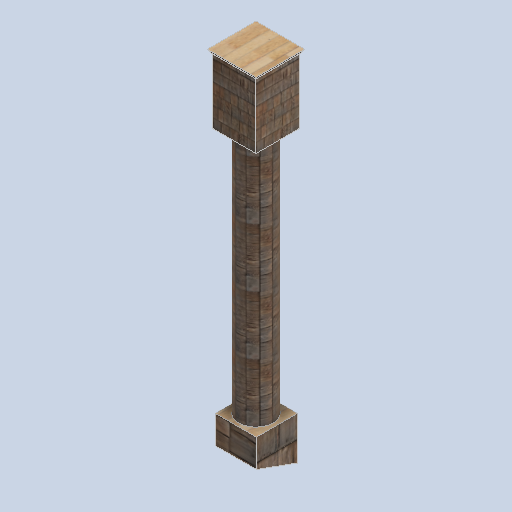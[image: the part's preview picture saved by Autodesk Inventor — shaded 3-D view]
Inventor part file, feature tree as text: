
AUTODESK INVENTOR PART (.ipt)
format: ipt  version: 2024.2 (Build 282272000, 272)  size: 172,544 bytes
history: native  units: in
note: dims shown in document units (in); Inventor stores cm internally (conversion verified against a paired STEP export)
features: sketch x5, other x3, plane x1
ambient origin geometry x8: Origin, YZ Plane, XZ Plane, XY Plane, X Axis, Y Axis, Z Axis, Center Point
bodies: Solid1 (feature_tree)
feature tree (9):
  other  "side_pillar_01_MIR2.ipt"
  other  "Solid1::side_pillar_01_MIR2.ipt"
  other  "TaggingFeature1"
  sketch  "Sketch1"  dims[d0=0.3937in]
  sketch  "Sketch2"
  sketch  "Sketch3"
  sketch  "Sketch4"
  sketch  "Sketch5"
  plane  "Work Plane3"
